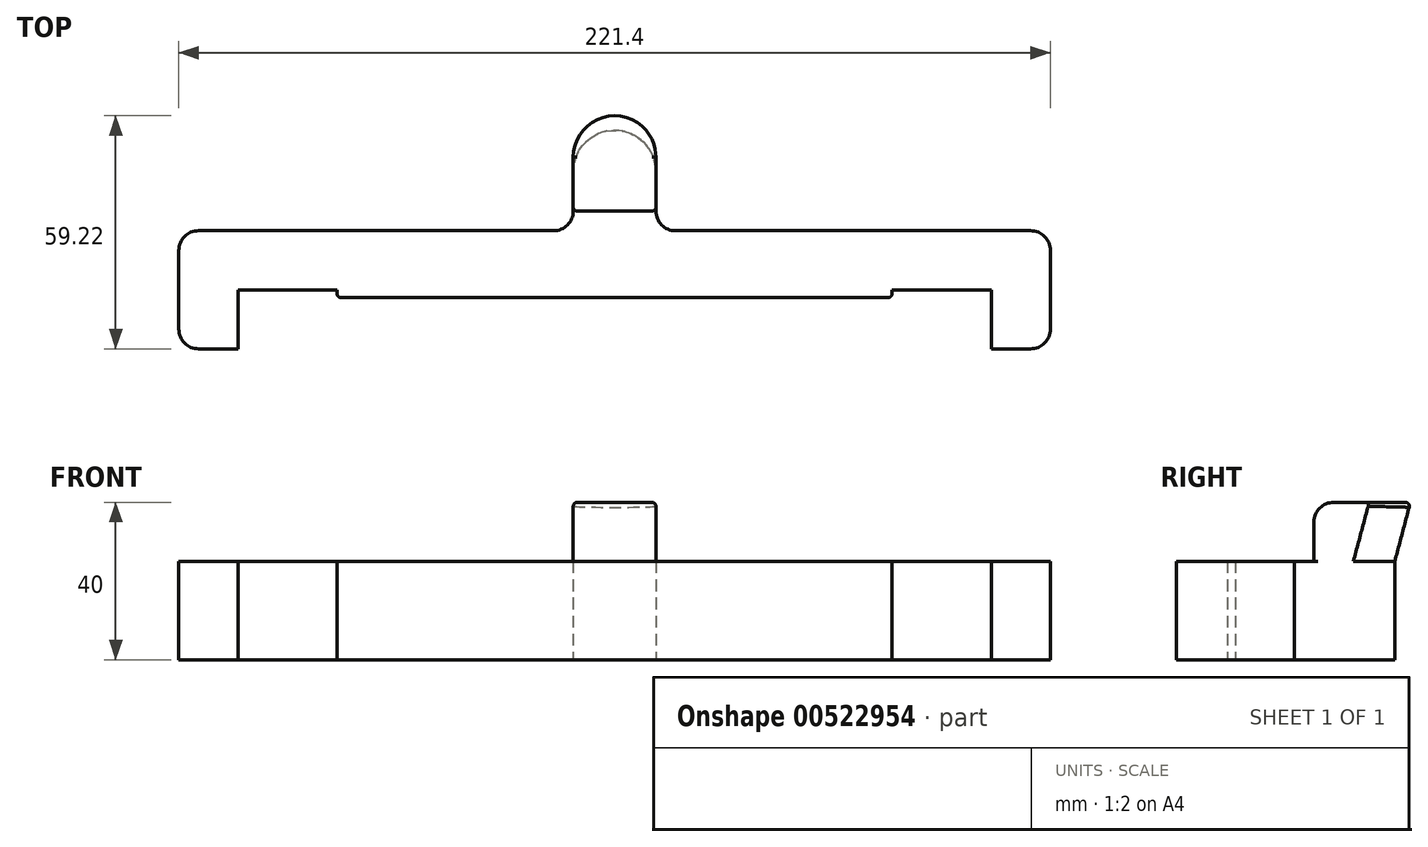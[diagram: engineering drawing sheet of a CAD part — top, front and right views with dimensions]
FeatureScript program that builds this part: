
annotation { "Feature Type Name" : "Feature", "Feature Type Description" : "" }
export const myFeature = defineFeature(function(context is Context, id is Id, definition is map)
    precondition{}
    {
        {
            var Q0;
            Q0=qCreatedBy(makeId("Top.planeOp"),FACE);
            var sketch = newSketch(context, id + "F0", { "sketchPlane" : qUnion([Q0])});
            skArc(sketch, "E0", {"start": v(10.5, 0) * mm, "mid": v(0, 10.5) * mm, "end": v(-10.5, 0) * mm});
            skLineSegment(sketch, "E1", {"start": v(-10.5, 0) * mm, "end": v(-10.5, -10) * mm});
            skLineSegment(sketch, "E2", {"start": v(-15.5, -15) * mm, "end": v(-105.7, -15) * mm});
            skLineSegment(sketch, "E3", {"start": v(-110.7, -20) * mm, "end": v(-110.7, -30) * mm});
            skLineSegment(sketch, "E4", {"start": v(-95.7, -30) * mm, "end": v(-70.5, -30) * mm});
            skLineSegment(sketch, "E5", {"start": v(-110.7, -30) * mm, "end": v(-110.7, -40) * mm});
            skLineSegment(sketch, "E6", {"start": v(-105.7, -45) * mm, "end": v(-95.7, -45) * mm});
            skLineSegment(sketch, "E7", {"start": v(-95.7, -45) * mm, "end": v(-95.7, -30) * mm});
            skLineSegment(sketch, "E8", {"start": v(-70.5, -30) * mm, "end": v(0, -30) * mm, "construction": true});
            skLineSegment(sketch, "E9", {"start": v(-70.5, -30) * mm, "end": v(-70.5, -31) * mm});
            skLineSegment(sketch, "E10", {"start": v(-69.5, -32) * mm, "end": v(0, -32) * mm});
            skPoint(sketch, "E11.visualSharp", {"position": v(-10.5, -15) * mm});
            skArc(sketch, "E11.filletArc", {"start": v(-15.5, -15) * mm, "mid": v(-11.96, -13.54) * mm, "end": v(-10.5, -10) * mm});
            skPoint(sketch, "E12.visualSharp", {"position": v(-110.7, -15) * mm});
            skArc(sketch, "E12.filletArc", {"start": v(-105.7, -15) * mm, "mid": v(-109.24, -16.46) * mm, "end": v(-110.7, -20) * mm});
            skPoint(sketch, "E13.visualSharp", {"position": v(-110.7, -45) * mm});
            skArc(sketch, "E13.filletArc", {"start": v(-110.7, -40) * mm, "mid": v(-109.24, -43.54) * mm, "end": v(-105.7, -45) * mm});
            skPoint(sketch, "E14.visualSharp", {"position": v(-70.5, -32) * mm});
            skArc(sketch, "E14.filletArc", {"start": v(-70.5, -31) * mm, "mid": v(-70.2, -31.7) * mm, "end": v(-69.5, -32) * mm});
            skLineSegment(sketch, "E15.MirrorCS", {"start": v(69.5, -32) * mm, "end": v(0, -32) * mm});
            skArc(sketch, "E16.MirrorCS", {"start": v(70.5, -31) * mm, "mid": v(70.2, -31.7) * mm, "end": v(69.5, -32) * mm});
            skLineSegment(sketch, "E17.MirrorCS", {"start": v(70.5, -30) * mm, "end": v(70.5, -31) * mm});
            skLineSegment(sketch, "E18.MirrorCS", {"start": v(95.7, -30) * mm, "end": v(70.5, -30) * mm});
            skLineSegment(sketch, "E19.MirrorCS", {"start": v(95.7, -45) * mm, "end": v(95.7, -30) * mm});
            skLineSegment(sketch, "E20.MirrorCS", {"start": v(105.7, -45) * mm, "end": v(95.7, -45) * mm});
            skArc(sketch, "E21.MirrorCS", {"start": v(110.7, -40) * mm, "mid": v(109.24, -43.54) * mm, "end": v(105.7, -45) * mm});
            skLineSegment(sketch, "E22.MirrorCS", {"start": v(110.7, -30) * mm, "end": v(110.7, -40) * mm});
            skLineSegment(sketch, "E23.MirrorCS", {"start": v(110.7, -20) * mm, "end": v(110.7, -30) * mm});
            skArc(sketch, "E24.MirrorCS", {"start": v(105.7, -15) * mm, "mid": v(109.24, -16.46) * mm, "end": v(110.7, -20) * mm});
            skLineSegment(sketch, "E25.MirrorCS", {"start": v(15.5, -15) * mm, "end": v(105.7, -15) * mm});
            skArc(sketch, "E26.MirrorCS", {"start": v(15.5, -15) * mm, "mid": v(11.96, -13.54) * mm, "end": v(10.5, -10) * mm});
            skLineSegment(sketch, "E27.MirrorCS", {"start": v(10.5, 0) * mm, "end": v(10.5, -10) * mm});
            skSolve(sketch);
        }
        {
            var Q0;
            Q0 = qSketchRegion(id + "F0", true);
            extrude(context, id + "F1", {"entities" : qUnion([Q0]), "depth" : 25 * mm, "offsetDistance" : 25 * mm});
        }
        {
            var Q0;
            Q0=makeQuery(id+"F1.opExtrude","CAP_FACE",FACE,{"disambiguationData":[OSD([sQuery(id+"F0.wireOp",EDGE,"E0"),sQuery(id+"F0.wireOp",EDGE,"E1"),sQuery(id+"F0.wireOp",EDGE,"E2"),sQuery(id+"F0.wireOp",EDGE,"E3"),sQuery(id+"F0.wireOp",EDGE,"E4"),sQuery(id+"F0.wireOp",EDGE,"E5"),sQuery(id+"F0.wireOp",EDGE,"E6"),sQuery(id+"F0.wireOp",EDGE,"E7"),sQuery(id+"F0.wireOp",EDGE,"E9"),sQuery(id+"F0.wireOp",EDGE,"E10"),sQuery(id+"F0.wireOp",EDGE,"E11.filletArc"),sQuery(id+"F0.wireOp",EDGE,"E12.filletArc"),sQuery(id+"F0.wireOp",EDGE,"E13.filletArc"),sQuery(id+"F0.wireOp",EDGE,"E14.filletArc"),sQuery(id+"F0.wireOp",EDGE,"E15.MirrorCS"),sQuery(id+"F0.wireOp",EDGE,"E16.MirrorCS"),sQuery(id+"F0.wireOp",EDGE,"E17.MirrorCS"),sQuery(id+"F0.wireOp",EDGE,"E18.MirrorCS"),sQuery(id+"F0.wireOp",EDGE,"E19.MirrorCS"),sQuery(id+"F0.wireOp",EDGE,"E20.MirrorCS"),sQuery(id+"F0.wireOp",EDGE,"E21.MirrorCS"),sQuery(id+"F0.wireOp",EDGE,"E22.MirrorCS"),sQuery(id+"F0.wireOp",EDGE,"E23.MirrorCS"),sQuery(id+"F0.wireOp",EDGE,"E24.MirrorCS"),sQuery(id+"F0.wireOp",EDGE,"E25.MirrorCS"),sQuery(id+"F0.wireOp",EDGE,"E26.MirrorCS"),sQuery(id+"F0.wireOp",EDGE,"E27.MirrorCS")])],"isStart":false});
            var sketch = newSketch(context, id + "F2", { "sketchPlane" : qUnion([Q0])});
            skLineSegment(sketch, "E28.bottom", {"start": v(-10.5, 0) * mm, "end": v(10.5, 0) * mm});
            skLineSegment(sketch, "E28.top", {"start": v(-10.5, -10) * mm, "end": v(10.5, -10) * mm});
            skLineSegment(sketch, "E28.left", {"start": v(-10.5, 0) * mm, "end": v(-10.5, -10) * mm});
            skLineSegment(sketch, "E28.right", {"start": v(10.5, 0) * mm, "end": v(10.5, -10) * mm});
            skSolve(sketch);
        }
        {
            var Q0;
            Q0 = qSketchRegion(id + "F2", true);
            extrude(context, id + "F3", {"entities" : qUnion([Q0]), "operationType" : NewBodyOperationType.ADD, "depth" : 15 * mm, "offsetDistance" : 25 * mm});
        }
        {
            var Q0;
            Q0=qCreatedBy(makeId("Right.planeOp"),FACE);
            var sketch = newSketch(context, id + "F4", { "sketchPlane" : qUnion([Q0])});
            skLineSegment(sketch, "E29", {"start": v(10.5, 25) * mm, "end": v(10.5, 0) * mm, "construction": true});
            skPoint(sketch, "E30.0", {"position": v(0, 40) * mm});
            skLineSegment(sketch, "E31", {"start": v(10.5, 25) * mm, "end": v(14.52, 40) * mm, "construction": true});
            skSolve(sketch);
        }
        {
            var Q0;
            Q0=makeQuery(id+"F3.opExtrude","CAP_FACE",FACE,{"disambiguationData":[OSD([sQuery(id+"F2.wireOp",EDGE,"E28.bottom"),sQuery(id+"F2.wireOp",EDGE,"E28.top"),sQuery(id+"F2.wireOp",EDGE,"E28.left"),sQuery(id+"F2.wireOp",EDGE,"E28.right")])],"isStart":false});
            var sketch = newSketch(context, id + "F5", { "sketchPlane" : qUnion([Q0])});
            skPoint(sketch, "E32.0", {"position": v(0, 14.52) * mm});
            skArc(sketch, "E33", {"start": v(10.5, 4.02) * mm, "mid": v(0, 14.52) * mm, "end": v(-10.5, 4.02) * mm});
            skLineSegment(sketch, "E34", {"start": v(-10.5, 4.02) * mm, "end": v(-10.5, -10) * mm});
            skLineSegment(sketch, "E35", {"start": v(-10.5, -10) * mm, "end": v(10.5, -10) * mm});
            skLineSegment(sketch, "E36", {"start": v(10.5, -10) * mm, "end": v(10.5, 4.02) * mm});
            skLineSegment(sketch, "E37", {"start": v(-10.5, 4.02) * mm, "end": v(10.5, 4.02) * mm});
            skSolve(sketch);
        }
        {
            var Q0;
            Q0=makeQuery(id+"F3.boolean.opBoolean","MERGE",FACE,{"derivedFrom":[makeQuery(id+"F1.opExtrude","SWEPT_FACE",FACE,{"disambiguationData":[OSD([sQuery(id+"F0.wireOp",EDGE,"E27.MirrorCS")])]}),makeQuery(id+"F3.opExtrude","SWEPT_FACE",FACE,{"disambiguationData":[OSD([sQuery(id+"F2.wireOp",EDGE,"E28.right")])]})]});
            var sketch = newSketch(context, id + "F6", { "sketchPlane" : qUnion([Q0])});
            skPoint(sketch, "E38.0", {"position": v(4.02, 40) * mm});
            skPoint(sketch, "E39.0", {"position": v(0, 25) * mm});
            skPoint(sketch, "E40.0", {"position": v(0, 40) * mm});
            skLineSegment(sketch, "E41", {"start": v(0, 40) * mm, "end": v(4.02, 40) * mm});
            skLineSegment(sketch, "E42", {"start": v(0, 25) * mm, "end": v(4.02, 40) * mm});
            skSolve(sketch);
        }
        {
            var Q0;
            Q0=makeQuery(id+"F6.imprint","IMPRINT",FACE,{"disambiguationData":[TD([[makeQuery(id+"F6.imprint","IMPRINT",EDGE,{"derivedFrom":sQuery(id+"F6.wireOp",EDGE,"E41")}),-1.0]])]});
            var Q1;
            Q1=makeQuery(id+"F3.boolean.opBoolean","MERGE",FACE,{"derivedFrom":[makeQuery(id+"F1.opExtrude","SWEPT_FACE",FACE,{"disambiguationData":[OSD([sQuery(id+"F0.wireOp",EDGE,"E1")])]}),makeQuery(id+"F3.opExtrude","SWEPT_FACE",FACE,{"disambiguationData":[OSD([sQuery(id+"F2.wireOp",EDGE,"E28.left")])]})]});
            extrude(context, id + "F7", {"entities" : qUnion([Q0]), "operationType" : NewBodyOperationType.ADD, "endBound" : BoundingType.UP_TO_SURFACE, "oppositeDirection" : true, "depth" : 25 * mm, "endBoundEntityFace" : qUnion([Q1]), "offsetDistance" : 25 * mm});
        }
        {
            var Q1;
            {var subQ0=sQuery(id+"F0.wireOp",EDGE,"E1");var subQ1=sQuery(id+"F0.wireOp",EDGE,"E27.MirrorCS");var subQ2=sQuery(id+"F0.wireOp",EDGE,"E0");Q1=makeQuery(id+"F3.boolean.opBoolean","SPLIT",FACE,{"disambiguationData":[TD([makeQuery(id+"F1.opExtrude","SWEPT_FACE",FACE,{"disambiguationData":[OSD([subQ2])]})])],"derivedFrom":makeQuery(id+"F1.opExtrude","CAP_FACE",FACE,{"disambiguationData":[OSD([subQ2,subQ0,sQuery(id+"F0.wireOp",EDGE,"E2"),sQuery(id+"F0.wireOp",EDGE,"E3"),sQuery(id+"F0.wireOp",EDGE,"E4"),sQuery(id+"F0.wireOp",EDGE,"E5"),sQuery(id+"F0.wireOp",EDGE,"E6"),sQuery(id+"F0.wireOp",EDGE,"E7"),sQuery(id+"F0.wireOp",EDGE,"E9"),sQuery(id+"F0.wireOp",EDGE,"E10"),sQuery(id+"F0.wireOp",EDGE,"E11.filletArc"),sQuery(id+"F0.wireOp",EDGE,"E12.filletArc"),sQuery(id+"F0.wireOp",EDGE,"E13.filletArc"),sQuery(id+"F0.wireOp",EDGE,"E14.filletArc"),sQuery(id+"F0.wireOp",EDGE,"E15.MirrorCS"),sQuery(id+"F0.wireOp",EDGE,"E16.MirrorCS"),sQuery(id+"F0.wireOp",EDGE,"E17.MirrorCS"),sQuery(id+"F0.wireOp",EDGE,"E18.MirrorCS"),sQuery(id+"F0.wireOp",EDGE,"E19.MirrorCS"),sQuery(id+"F0.wireOp",EDGE,"E20.MirrorCS"),sQuery(id+"F0.wireOp",EDGE,"E21.MirrorCS"),sQuery(id+"F0.wireOp",EDGE,"E22.MirrorCS"),sQuery(id+"F0.wireOp",EDGE,"E23.MirrorCS"),sQuery(id+"F0.wireOp",EDGE,"E24.MirrorCS"),sQuery(id+"F0.wireOp",EDGE,"E25.MirrorCS"),sQuery(id+"F0.wireOp",EDGE,"E26.MirrorCS"),subQ1])],"isStart":false})});}
            var Q2;
            Q2=makeQuery(id+"F5.imprint","IMPRINT",FACE,{"disambiguationData":[TD([[makeQuery(id+"F5.imprint","IMPRINT",EDGE,{"derivedFrom":sQuery(id+"F5.wireOp",EDGE,"E33")}),1.0]])]});
            loft(context, id + "F8", {"operationType" : NewBodyOperationType.ADD, "sheetProfilesArray" : [{ "sheetProfileEntities" : qUnion([Q1]) }, { "sheetProfileEntities" : qUnion([Q2]) }]});
        }
        {
            var Q0;
            Q0=makeQuery(id+"F3.opExtrude","CAP_EDGE",EDGE,{"disambiguationData":[OSD([sQuery(id+"F2.wireOp",EDGE,"E28.top")])],"isStart":false});
            var Q1;
            Q1=makeQuery(id+"F3.opExtrude","CAP_EDGE",EDGE,{"disambiguationData":[OSD([sQuery(id+"F2.wireOp",EDGE,"E28.top")])],"isStart":true});
            fillet(context, id + "F9", {"entities" : qUnion([Q0, Q1]), "radius" : 5 * mm, "tangentPropagation" : true, "allowEdgeOverflow" : false});
        }
        {
            var Q0;
            Q0=makeQuery(id+"F8.opLoft","MID_CAP_EDGE",EDGE,{"disambiguationData":[OSD([sQuery(id+"F5.wireOp",EDGE,"E33"),sQuery(id+"F5.wireOp",EDGE,"E34"),sQuery(id+"F5.wireOp",EDGE,"E36")])],"capPos":1.0});
            fillet(context, id + "F10", {"entities" : qUnion([Q0]), "radius" : 1 * mm, "tangentPropagation" : true, "allowEdgeOverflow" : false});
        }
    });
